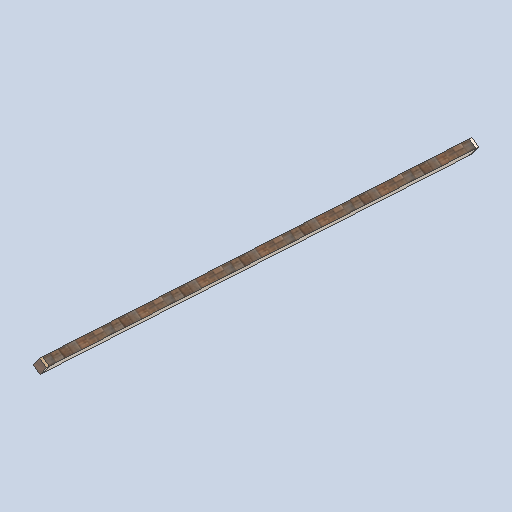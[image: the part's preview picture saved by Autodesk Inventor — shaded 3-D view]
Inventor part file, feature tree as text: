
AUTODESK INVENTOR PART (.ipt)
format: ipt  version: 2024.2 (Build 282272000, 272)  size: 131,072 bytes
history: native  units: in
note: dims shown in document units (in); Inventor stores cm internally (conversion verified against a paired STEP export)
features: sketch x4, other x3, plane x2
ambient origin geometry x8: Origin, YZ Plane, XZ Plane, XY Plane, X Axis, Y Axis, Z Axis, Center Point
bodies: Solid1 (feature_tree)
feature tree (9):
  other  "support_beam_segment_0104_MIR.ipt"
  other  "Solid1::support_beam_segment_0104_MIR.ipt"
  other  "TaggingFeature1"
  sketch  "Sketch1"  dims[d0=0.3937in]
  sketch  "Sketch2"
  sketch  "Sketch3"
  sketch  "Sketch4"
  plane  "Work Plane1"
  plane  "Work Plane2"
